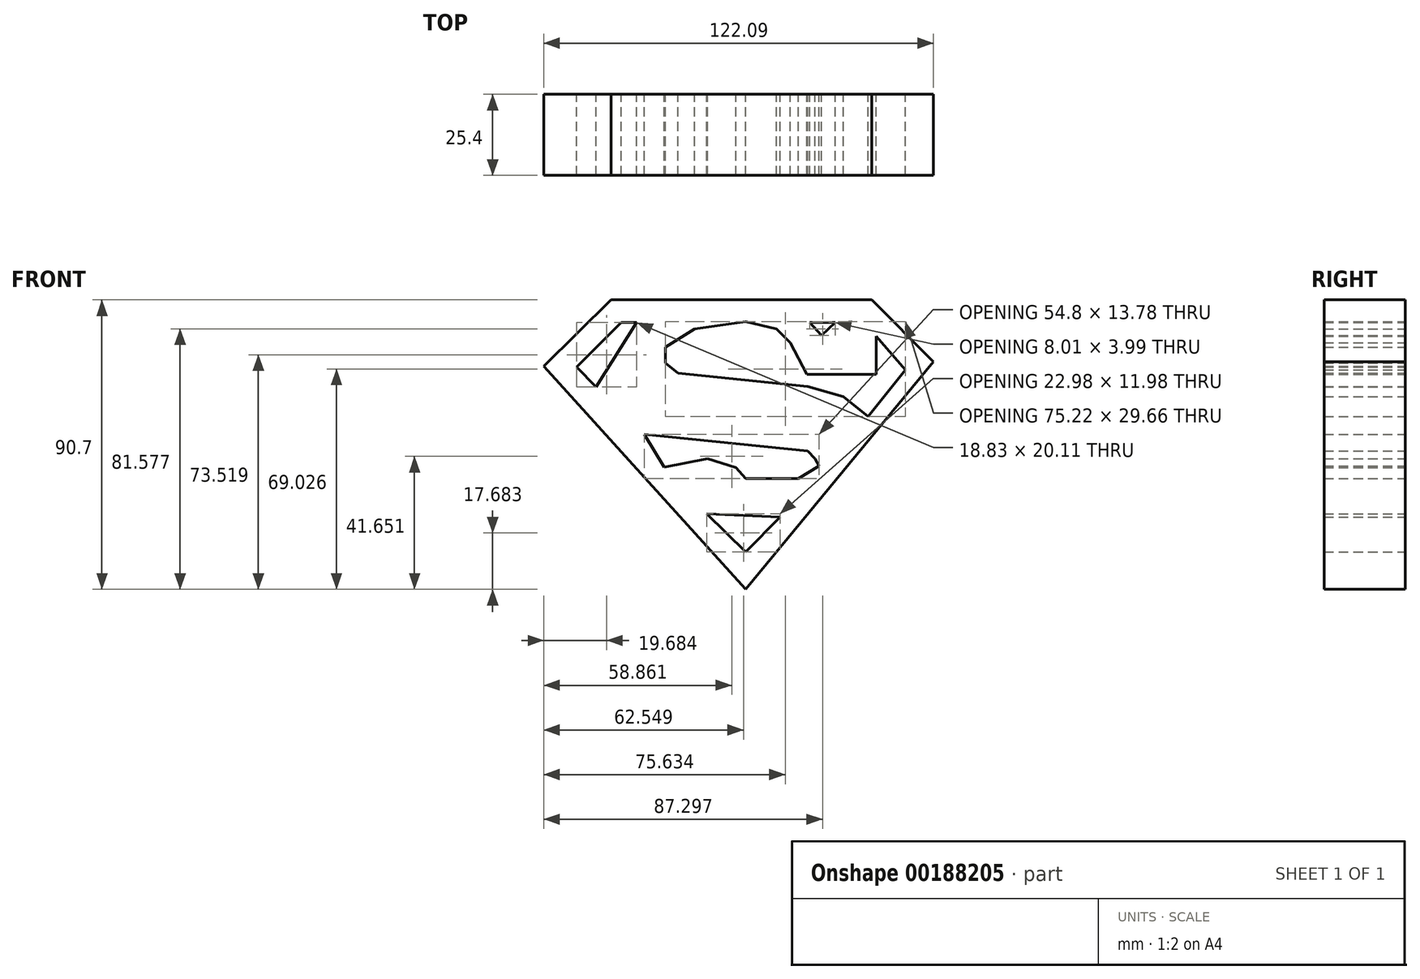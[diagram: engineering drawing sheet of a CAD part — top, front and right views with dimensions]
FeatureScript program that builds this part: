
annotation { "Feature Type Name" : "Feature", "Feature Type Description" : "" }
export const myFeature = defineFeature(function(context is Context, id is Id, definition is map)
    precondition{}
    {
        {
            var Q0;
            Q0=qCreatedBy(makeId("Front.planeOp"),FACE);
            var sketch = newSketch(context, id + "F0", { "sketchPlane" : qUnion([Q0])});
            skLineSegment(sketch, "E0", {"start": v(-42.1, 49.77) * mm, "end": v(39.48, 49.77) * mm});
            skLineSegment(sketch, "E1", {"start": v(39.48, 49.77) * mm, "end": v(58.88, 30.38) * mm});
            skLineSegment(sketch, "E2", {"start": v(58.88, 30.38) * mm, "end": v(0, -40.93) * mm});
            skLineSegment(sketch, "E3", {"start": v(-42.1, 49.77) * mm, "end": v(-63.2, 28.95) * mm});
            skLineSegment(sketch, "E4", {"start": v(-63.2, 28.95) * mm, "end": v(0, -40.93) * mm});
            skLineSegment(sketch, "E5", {"start": v(-38.96, 42.64) * mm, "end": v(-34.11, 42.64) * mm});
            skLineSegment(sketch, "E6", {"start": v(-38.96, 42.64) * mm, "end": v(-52.94, 28.67) * mm});
            skLineSegment(sketch, "E7", {"start": v(-52.94, 28.67) * mm, "end": v(-46.8, 22.53) * mm});
            skLineSegment(sketch, "E8", {"start": v(-46.8, 22.53) * mm, "end": v(-34.11, 42.64) * mm});
            skLineSegment(sketch, "E9", {"start": v(20.08, 42.64) * mm, "end": v(23.8, 38.65) * mm});
            skLineSegment(sketch, "E10", {"start": v(23.8, 38.65) * mm, "end": v(28.1, 42.64) * mm});
            skLineSegment(sketch, "E11", {"start": v(28.1, 42.64) * mm, "end": v(20.08, 42.64) * mm});
            skLineSegment(sketch, "E12", {"start": v(-12.15, -17.26) * mm, "end": v(0, -29.24) * mm});
            skLineSegment(sketch, "E13", {"start": v(0, -29.24) * mm, "end": v(10.83, -18.26) * mm});
            skLineSegment(sketch, "E14", {"start": v(10.83, -18.26) * mm, "end": v(-12.15, -17.26) * mm});
            skLineSegment(sketch, "E15", {"start": v(40.9, 38.36) * mm, "end": v(50.03, 27.81) * mm});
            skLineSegment(sketch, "E16", {"start": v(50.03, 27.81) * mm, "end": v(38.34, 13.26) * mm});
            skLineSegment(sketch, "E17", {"start": v(40.9, 38.36) * mm, "end": v(40.9, 26.38) * mm});
            skLineSegment(sketch, "E18", {"start": v(40.9, 26.38) * mm, "end": v(19.23, 26.38) * mm});
            skLineSegment(sketch, "E19", {"start": v(-32.4, 8.7) * mm, "end": v(-25.56, -2.7) * mm});
            skLineSegment(sketch, "E20", {"start": v(-31.75, 7.6) * mm, "end": v(19.51, 2.42) * mm});
            skLineSegment(sketch, "E21", {"start": v(19.51, 2.42) * mm, "end": v(21.7, 0) * mm});
            skLineSegment(sketch, "E22", {"start": v(21.7, 0) * mm, "end": v(23.05, -2.24) * mm});
            skLineSegment(sketch, "E23", {"start": v(23.05, -2.24) * mm, "end": v(16.5, -6.17) * mm});
            skLineSegment(sketch, "E24", {"start": v(16.5, -6.17) * mm, "end": v(0, -6.17) * mm});
            skLineSegment(sketch, "E25", {"start": v(0, -6.17) * mm, "end": v(-3.04, -2.8) * mm});
            skLineSegment(sketch, "E26", {"start": v(-3.04, -2.8) * mm, "end": v(-11.86, 0) * mm});
            skLineSegment(sketch, "E27", {"start": v(-11.86, 0) * mm, "end": v(-25.56, -2.7) * mm});
            skLineSegment(sketch, "E28", {"start": v(38.34, 13.26) * mm, "end": v(30.67, 19.43) * mm});
            skLineSegment(sketch, "E29", {"start": v(30.67, 19.43) * mm, "end": v(19.51, 22.68) * mm});
            skLineSegment(sketch, "E30", {"start": v(19.51, 22.68) * mm, "end": v(7.03, 23.94) * mm});
            skLineSegment(sketch, "E31", {"start": v(7.03, 23.94) * mm, "end": v(-16.35, 26.3) * mm});
            skLineSegment(sketch, "E32", {"start": v(-16.35, 26.3) * mm, "end": v(-21.21, 26.8) * mm});
            skLineSegment(sketch, "E33", {"start": v(-21.21, 26.8) * mm, "end": v(-25.18, 29.99) * mm});
            skLineSegment(sketch, "E34", {"start": v(-25.18, 29.99) * mm, "end": v(-25.18, 34.94) * mm});
            skLineSegment(sketch, "E35", {"start": v(-25.18, 34.94) * mm, "end": v(-15.97, 40.65) * mm});
            skLineSegment(sketch, "E36", {"start": v(-15.97, 40.65) * mm, "end": v(0, 42.93) * mm});
            skLineSegment(sketch, "E37", {"start": v(0, 42.93) * mm, "end": v(9.7, 40.65) * mm});
            skLineSegment(sketch, "E38", {"start": v(9.7, 40.65) * mm, "end": v(13.98, 36.37) * mm});
            skLineSegment(sketch, "E39", {"start": v(13.98, 36.37) * mm, "end": v(19.23, 26.38) * mm});
            skSolve(sketch);
        }
        {
            var Q0;
            Q0=makeQuery(id+"F0.imprint","IMPRINT",FACE,{"disambiguationData":[TD([[makeQuery(id+"F0.imprint","IMPRINT",EDGE,{"derivedFrom":sQuery(id+"F0.wireOp",EDGE,"E0")}),-1.0]])]});
            extrude(context, id + "F1", {"entities" : qUnion([Q0]), "depth" : 25.4 * mm});
        }
    });
